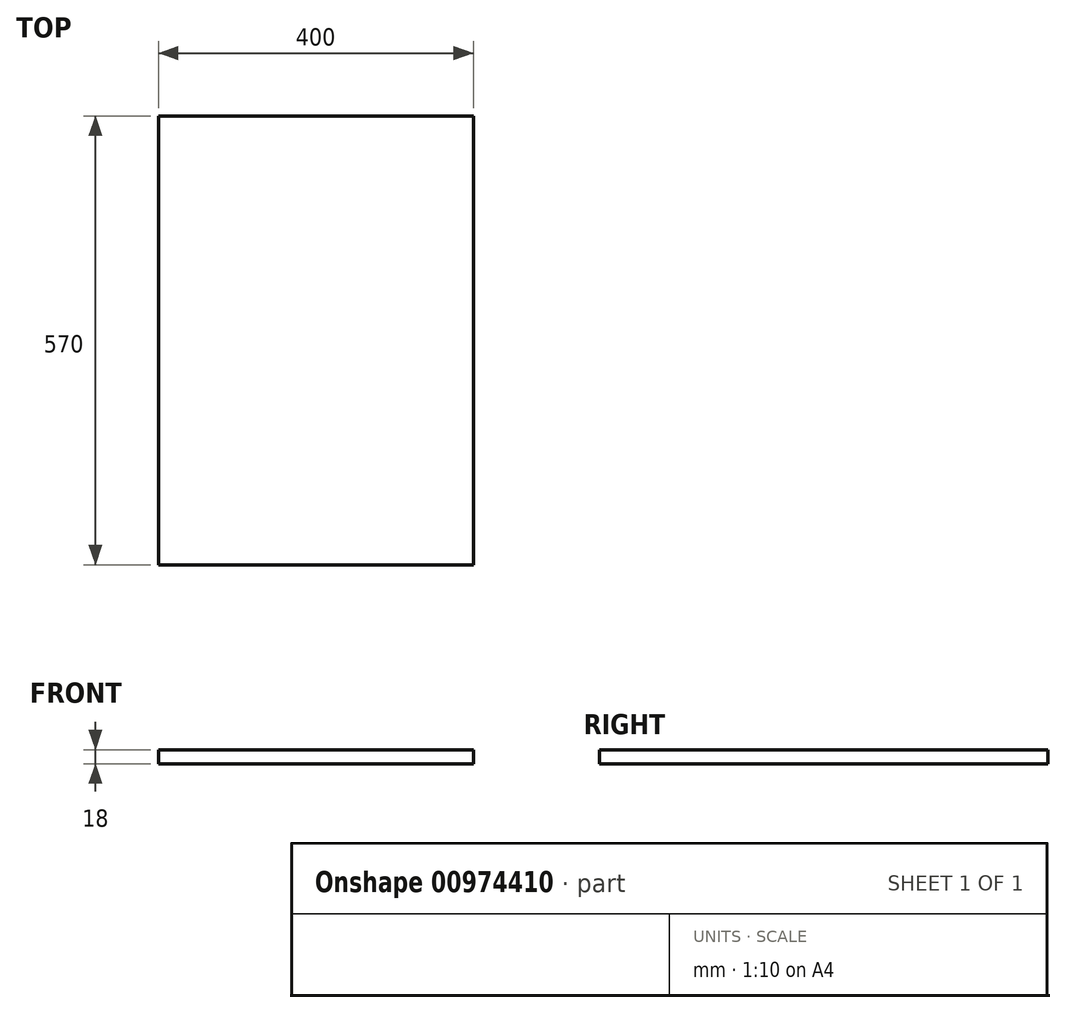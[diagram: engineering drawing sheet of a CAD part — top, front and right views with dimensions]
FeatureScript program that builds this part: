
annotation { "Feature Type Name" : "Feature", "Feature Type Description" : "" }
export const myFeature = defineFeature(function(context is Context, id is Id, definition is map)
    precondition{}
    {
        {
            var Q0;
            Q0=qCreatedBy(makeId("Top.planeOp"),FACE);
            var sketch = newSketch(context, id + "F0", { "sketchPlane" : qUnion([Q0])});
            skLineSegment(sketch, "E0.bottom", {"start": v(200, 285) * mm, "end": v(-200, 285) * mm});
            skLineSegment(sketch, "E0.top", {"start": v(200, -285) * mm, "end": v(-200, -285) * mm});
            skLineSegment(sketch, "E0.left", {"start": v(200, 285) * mm, "end": v(200, -285) * mm});
            skLineSegment(sketch, "E0.right", {"start": v(-200, 285) * mm, "end": v(-200, -285) * mm});
            skPoint(sketch, "E0.middle", {"position": v(0, 0) * mm});
            skSolve(sketch);
        }
        {
            var Q0;
            Q0=makeQuery(id+"F0.imprint","IMPRINT",FACE,{"disambiguationData":[TD([[makeQuery(id+"F0.imprint","IMPRINT",EDGE,{"derivedFrom":sQuery(id+"F0.wireOp",EDGE,"E0.bottom")}),1.0]])]});
            extrude(context, id + "F1", {"entities" : qUnion([Q0]), "depth" : 18 * mm, "offsetDistance" : 25 * mm});
        }
    });
